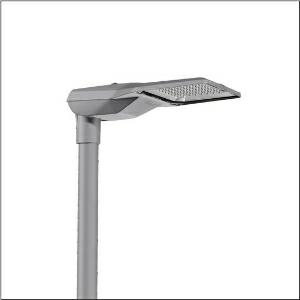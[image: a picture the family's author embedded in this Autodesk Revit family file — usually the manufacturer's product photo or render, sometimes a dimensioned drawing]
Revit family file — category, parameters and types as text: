
# Revit family: streetlight_sl_21_midi___st0_5a_5xe3b43s08mb_23ad
name_source: partatom
category: Lighting Fixtures
units: mm (PartAtom-declared; Revit-internal decimal feet)

## family parameters
Cut with Voids When Loaded = No
Host = Face
Light Source = No
Part Type = Normal
Room Calculation Point = No
Round Connector Dimension = Use Diameter
Shared = No

## types (1)
- --- (1 x LED, 20180 lm, 147 W, 4000K)
    Apparent Load = 147 VA
    CIE Flux Codes = 41 75 97 100 100
    Color Rendering = 70
    Color Temperature = 4000K
    Default Elevation = 1800 mm
    Description = Streetlight SL 21 midi, mast luminaire, primary light control with lens, of PMMA, primary optical cover: cover, of toughened safety glass, transparent, light distribution: ST0.5a, light emission: direct distribution, primary light characteristic: asymmetric, installation type: side-entry, post-top, LED, High Power LED, rated luminous flux: 20.180lm, luminous efficacy: 137lm/W, light colour: 740, colour temperature: 4000K, control gear: D4i, control: overheat protection, constant luminous flux control, time-dependent luminous flux control, flexible luminous flux parameterisation, pre-setting: logarithmic dimming characteristic, mains connection: 230..240V, AC, 50/60Hz, start of lifetime: 147W, end of service life: 155W, reduction: 65W, luminaire housing, of diecast aluminium, powder-coated, SITECO metallic grey (DB 702S), corrosivity category C5 high according to DIN EN ISO 12944, please order mast flange separately, inclination adjustable: 0°, 5°, 10°, 15°, sealing non-destructively replaceable, multi-level sealing system, length: 644mm, width: 335mm, height: 110mm, mast flange for spigot size: 42mm (side-entry): 5XC10008XM4, 60/48mm (side-entry/post-top): 5XC10108XM2, 76/60mm (side-entry/post-top): 5XC10108XM1, mounting height: 4..8m, Smart Interface above, protection rating (complete): IP66, insulation class (complete): insulation class II (safety insulation), certification: CE, ENEC, ENEC+, VDE, impact resistance: IK10, permissible operating ambient temperature for outdoor applications: -40..+50°C, standard-compliant lighting for roads and squares, packaging unit: 1 piece

Light Distribution: ST0.5a
    Height = 111 mm
    Lamp = 1 x LED
    Lamp Light Flux = 20180 lm
    Lamp Power = 147 W
    Lamp count = 1
    Length = 644 mm
    Luminous efficacy = 137 lm/W
    Manufacturer = Siteco
    ModVariant = No
    Model = 5XE3B43S08MB
    Number of Poles = 1
    OnlyDefault = Yes
    Power Factor = 1
    Product Name = Streetlight SL 21 midi | ST0.5a
    Product group = mast luminaire | pylon top
    ProductGroupID = 6100
    Protection Class = Protection class II
    Protection Degree = IP 66
    RLX_Detail_Level = 1
    RLX_Emergency_Light_Flux = 0 lm
    RLX_Emergency_Type = 0
    RLX_Emergency_Type_DB = No
    RlxData = <blob elided: 37909 chars, md5=50b4ece0>
    Socket = socket
    Standby Power = 0 W
    System Light Flux = 20180 lm
    System Power = 147 W
    Type Comments = factory setting: luminous flux: 100 % | dim-lin: 254 | 750 mA
    Type Image = l_1004302.jpg
    URL = http://relux.com
    VarID = @adj_189147
    Voltage = 0 V
    Weight = 0.00 kg
    Width = 336 mm

## geometry (parser evidence)
native form markers: Blend x4, Sweep x9
no freeform markers — native parametric forms only
